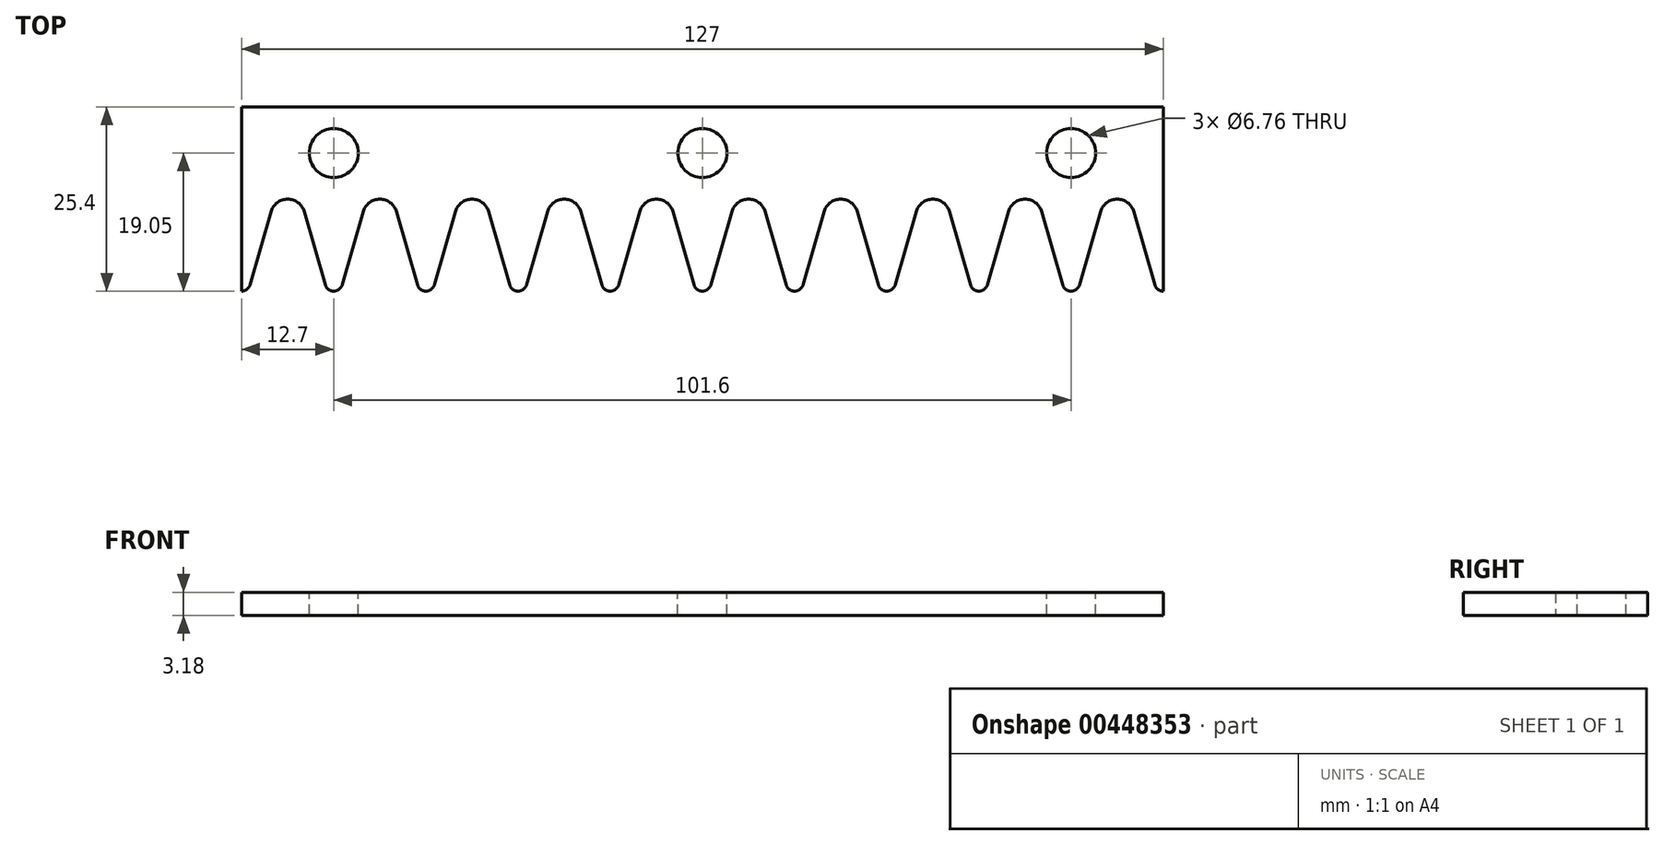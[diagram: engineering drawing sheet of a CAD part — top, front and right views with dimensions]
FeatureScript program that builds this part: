
annotation { "Feature Type Name" : "Feature", "Feature Type Description" : "" }
export const myFeature = defineFeature(function(context is Context, id is Id, definition is map)
    precondition{}
    {
        {
            var Q0;
            Q0=qCreatedBy(makeId("Top.planeOp"),FACE);
            var sketch = newSketch(context, id + "F0", { "sketchPlane" : qUnion([Q0])});
            skLineSegment(sketch, "E0.bottom", {"start": v(0, 0) * mm, "end": v(-127, 0) * mm, "construction": true});
            skLineSegment(sketch, "E0.top", {"start": v(0, 12.7) * mm, "end": v(-127, 12.7) * mm});
            skLineSegment(sketch, "E0.left", {"start": v(0, 0) * mm, "end": v(0, 12.7) * mm});
            skLineSegment(sketch, "E0.right", {"start": v(-127, 0) * mm, "end": v(-127, 12.7) * mm});
            skLineSegment(sketch, "E1", {"start": v(-127, 0) * mm, "end": v(-127, -12.7) * mm});
            skArc(sketch, "E2", {"start": v(-122.94, -1.72) * mm, "mid": v(-120.65, 0) * mm, "end": v(-118.36, -1.72) * mm});
            skLineSegment(sketch, "E3", {"start": v(-114.3, -12.7) * mm, "end": v(-114.3, 0) * mm});
            skLineSegment(sketch, "E4.1.0.0", {"start": v(-114.3, 0) * mm, "end": v(-114.3, -12.7) * mm});
            skLineSegment(sketch, "E4.direction1", {"start": v(-127, -12.7) * mm, "end": v(-114.3, -12.7) * mm, "construction": true});
            skLineSegment(sketch, "E5", {"start": v(-118.36, -1.72) * mm, "end": v(-115.44, -11.84) * mm});
            skArc(sketch, "E6", {"start": v(-125.86, -11.84) * mm, "mid": v(-126.28, -12.46) * mm, "end": v(-127, -12.7) * mm});
            skArc(sketch, "E7", {"start": v(-115.44, -11.84) * mm, "mid": v(-115.02, -12.46) * mm, "end": v(-114.3, -12.7) * mm});
            skLineSegment(sketch, "E8", {"start": v(-125.86, -11.84) * mm, "end": v(-122.94, -1.72) * mm});
            skLineSegment(sketch, "E9.1.0.1", {"start": v(-113.16, -11.84) * mm, "end": v(-110.24, -1.72) * mm});
            skArc(sketch, "E9.1.0.2", {"start": v(-110.24, -1.72) * mm, "mid": v(-107.95, 0) * mm, "end": v(-105.66, -1.72) * mm});
            skLineSegment(sketch, "E9.1.0.3", {"start": v(-105.66, -1.72) * mm, "end": v(-102.74, -11.84) * mm});
            skLineSegment(sketch, "E9.1.0.4", {"start": v(-101.6, 0) * mm, "end": v(-101.6, -12.7) * mm});
            skArc(sketch, "E9.1.0.5", {"start": v(-113.16, -11.84) * mm, "mid": v(-113.58, -12.46) * mm, "end": v(-114.3, -12.7) * mm});
            skArc(sketch, "E9.1.0.6", {"start": v(-102.74, -11.84) * mm, "mid": v(-102.32, -12.46) * mm, "end": v(-101.6, -12.7) * mm});
            skLineSegment(sketch, "E9.2.0.0", {"start": v(-101.6, 0) * mm, "end": v(-101.6, -12.7) * mm});
            skLineSegment(sketch, "E9.2.0.1", {"start": v(-100.46, -11.84) * mm, "end": v(-97.54, -1.72) * mm});
            skArc(sketch, "E9.2.0.2", {"start": v(-97.54, -1.72) * mm, "mid": v(-95.25, 0) * mm, "end": v(-92.96, -1.72) * mm});
            skLineSegment(sketch, "E9.2.0.3", {"start": v(-92.96, -1.72) * mm, "end": v(-90.04, -11.84) * mm});
            skLineSegment(sketch, "E9.2.0.4", {"start": v(-88.9, 0) * mm, "end": v(-88.9, -12.7) * mm});
            skArc(sketch, "E9.2.0.5", {"start": v(-100.46, -11.84) * mm, "mid": v(-100.88, -12.46) * mm, "end": v(-101.6, -12.7) * mm});
            skArc(sketch, "E9.2.0.6", {"start": v(-90.04, -11.84) * mm, "mid": v(-89.62, -12.46) * mm, "end": v(-88.9, -12.7) * mm});
            skLineSegment(sketch, "E9.3.0.0", {"start": v(-88.9, 0) * mm, "end": v(-88.9, -12.7) * mm});
            skLineSegment(sketch, "E9.3.0.1", {"start": v(-87.76, -11.84) * mm, "end": v(-84.84, -1.72) * mm});
            skArc(sketch, "E9.3.0.2", {"start": v(-84.84, -1.72) * mm, "mid": v(-82.55, 0) * mm, "end": v(-80.26, -1.72) * mm});
            skLineSegment(sketch, "E9.3.0.3", {"start": v(-80.26, -1.72) * mm, "end": v(-77.34, -11.84) * mm});
            skLineSegment(sketch, "E9.3.0.4", {"start": v(-76.2, 0) * mm, "end": v(-76.2, -12.7) * mm});
            skArc(sketch, "E9.3.0.5", {"start": v(-87.76, -11.84) * mm, "mid": v(-88.18, -12.46) * mm, "end": v(-88.9, -12.7) * mm});
            skArc(sketch, "E9.3.0.6", {"start": v(-77.34, -11.84) * mm, "mid": v(-76.92, -12.46) * mm, "end": v(-76.2, -12.7) * mm});
            skLineSegment(sketch, "E9.4.0.0", {"start": v(-76.2, 0) * mm, "end": v(-76.2, -12.7) * mm});
            skLineSegment(sketch, "E9.4.0.1", {"start": v(-75.06, -11.84) * mm, "end": v(-72.14, -1.72) * mm});
            skArc(sketch, "E9.4.0.2", {"start": v(-72.14, -1.72) * mm, "mid": v(-69.85, 0) * mm, "end": v(-67.56, -1.72) * mm});
            skLineSegment(sketch, "E9.4.0.3", {"start": v(-67.56, -1.72) * mm, "end": v(-64.64, -11.84) * mm});
            skLineSegment(sketch, "E9.4.0.4", {"start": v(-63.5, 0) * mm, "end": v(-63.5, -12.7) * mm});
            skArc(sketch, "E9.4.0.5", {"start": v(-75.06, -11.84) * mm, "mid": v(-75.48, -12.46) * mm, "end": v(-76.2, -12.7) * mm});
            skArc(sketch, "E9.4.0.6", {"start": v(-64.64, -11.84) * mm, "mid": v(-64.22, -12.46) * mm, "end": v(-63.5, -12.7) * mm});
            skLineSegment(sketch, "E9.5.0.0", {"start": v(-63.5, 0) * mm, "end": v(-63.5, -12.7) * mm});
            skLineSegment(sketch, "E9.5.0.1", {"start": v(-62.36, -11.84) * mm, "end": v(-59.44, -1.72) * mm});
            skArc(sketch, "E9.5.0.2", {"start": v(-59.44, -1.72) * mm, "mid": v(-57.15, 0) * mm, "end": v(-54.86, -1.72) * mm});
            skLineSegment(sketch, "E9.5.0.3", {"start": v(-54.86, -1.72) * mm, "end": v(-51.94, -11.84) * mm});
            skLineSegment(sketch, "E9.5.0.4", {"start": v(-50.8, 0) * mm, "end": v(-50.8, -12.7) * mm});
            skArc(sketch, "E9.5.0.5", {"start": v(-62.36, -11.84) * mm, "mid": v(-62.78, -12.46) * mm, "end": v(-63.5, -12.7) * mm});
            skArc(sketch, "E9.5.0.6", {"start": v(-51.94, -11.84) * mm, "mid": v(-51.52, -12.46) * mm, "end": v(-50.8, -12.7) * mm});
            skLineSegment(sketch, "E9.6.0.0", {"start": v(-50.8, 0) * mm, "end": v(-50.8, -12.7) * mm});
            skLineSegment(sketch, "E9.6.0.1", {"start": v(-49.66, -11.84) * mm, "end": v(-46.74, -1.72) * mm});
            skArc(sketch, "E9.6.0.2", {"start": v(-46.74, -1.72) * mm, "mid": v(-44.45, 0) * mm, "end": v(-42.16, -1.72) * mm});
            skLineSegment(sketch, "E9.6.0.3", {"start": v(-42.16, -1.72) * mm, "end": v(-39.24, -11.84) * mm});
            skLineSegment(sketch, "E9.6.0.4", {"start": v(-38.1, 0) * mm, "end": v(-38.1, -12.7) * mm});
            skArc(sketch, "E9.6.0.5", {"start": v(-49.66, -11.84) * mm, "mid": v(-50.08, -12.46) * mm, "end": v(-50.8, -12.7) * mm});
            skArc(sketch, "E9.6.0.6", {"start": v(-39.24, -11.84) * mm, "mid": v(-38.82, -12.46) * mm, "end": v(-38.1, -12.7) * mm});
            skLineSegment(sketch, "E9.7.0.0", {"start": v(-38.1, 0) * mm, "end": v(-38.1, -12.7) * mm});
            skLineSegment(sketch, "E9.7.0.1", {"start": v(-36.96, -11.84) * mm, "end": v(-34.04, -1.72) * mm});
            skArc(sketch, "E9.7.0.2", {"start": v(-34.04, -1.72) * mm, "mid": v(-31.75, 0) * mm, "end": v(-29.46, -1.72) * mm});
            skLineSegment(sketch, "E9.7.0.3", {"start": v(-29.46, -1.72) * mm, "end": v(-26.54, -11.84) * mm});
            skLineSegment(sketch, "E9.7.0.4", {"start": v(-25.4, 0) * mm, "end": v(-25.4, -12.7) * mm});
            skArc(sketch, "E9.7.0.5", {"start": v(-36.96, -11.84) * mm, "mid": v(-37.38, -12.46) * mm, "end": v(-38.1, -12.7) * mm});
            skArc(sketch, "E9.7.0.6", {"start": v(-26.54, -11.84) * mm, "mid": v(-26.12, -12.46) * mm, "end": v(-25.4, -12.7) * mm});
            skLineSegment(sketch, "E9.8.0.0", {"start": v(-25.4, 0) * mm, "end": v(-25.4, -12.7) * mm});
            skLineSegment(sketch, "E9.8.0.1", {"start": v(-24.26, -11.84) * mm, "end": v(-21.34, -1.72) * mm});
            skArc(sketch, "E9.8.0.2", {"start": v(-21.34, -1.72) * mm, "mid": v(-19.05, 0) * mm, "end": v(-16.76, -1.72) * mm});
            skLineSegment(sketch, "E9.8.0.3", {"start": v(-16.76, -1.72) * mm, "end": v(-13.84, -11.84) * mm});
            skLineSegment(sketch, "E9.8.0.4", {"start": v(-12.7, 0) * mm, "end": v(-12.7, -12.7) * mm});
            skArc(sketch, "E9.8.0.5", {"start": v(-24.26, -11.84) * mm, "mid": v(-24.68, -12.46) * mm, "end": v(-25.4, -12.7) * mm});
            skArc(sketch, "E9.8.0.6", {"start": v(-13.84, -11.84) * mm, "mid": v(-13.42, -12.46) * mm, "end": v(-12.7, -12.7) * mm});
            skLineSegment(sketch, "E9.9.0.0", {"start": v(-12.7, 0) * mm, "end": v(-12.7, -12.7) * mm});
            skLineSegment(sketch, "E9.9.0.1", {"start": v(-11.56, -11.84) * mm, "end": v(-8.64, -1.72) * mm});
            skArc(sketch, "E9.9.0.2", {"start": v(-8.64, -1.72) * mm, "mid": v(-6.35, 0) * mm, "end": v(-4.06, -1.72) * mm});
            skLineSegment(sketch, "E9.9.0.3", {"start": v(-4.06, -1.72) * mm, "end": v(-1.14, -11.84) * mm});
            skLineSegment(sketch, "E9.9.0.4", {"start": v(0, 0) * mm, "end": v(0, -12.7) * mm});
            skArc(sketch, "E9.9.0.5", {"start": v(-11.56, -11.84) * mm, "mid": v(-11.98, -12.46) * mm, "end": v(-12.7, -12.7) * mm});
            skArc(sketch, "E9.9.0.6", {"start": v(-1.14, -11.84) * mm, "mid": v(-0.72, -12.46) * mm, "end": v(0, -12.7) * mm});
            skSolve(sketch);
        }
        {
            var Q0;
            Q0=makeQuery(id+"F0.imprint","IMPRINT",FACE,{"disambiguationData":[TD([[makeQuery(id+"F0.imprint","IMPRINT",EDGE,{"derivedFrom":sQuery(id+"F0.wireOp",EDGE,"E0.top")}),1.0]])]});
            extrude(context, id + "F1", {"entities" : qUnion([Q0]), "depth" : 3.17 * mm});
        }
        {
            var Q0;
            Q0=makeQuery(id+"F1.opExtrude","CAP_FACE",FACE,{"disambiguationData":[OSD([sQuery(id+"F0.wireOp",EDGE,"E0.top"),sQuery(id+"F0.wireOp",EDGE,"E0.left"),sQuery(id+"F0.wireOp",EDGE,"E0.right"),sQuery(id+"F0.wireOp",EDGE,"E1"),sQuery(id+"F0.wireOp",EDGE,"PW4FySWp-zVU2-GpDa-Lfng-2MmFDWqlCH1t"),sQuery(id+"F0.wireOp",EDGE,"CtuzIzuM-RDB8-6xeh-k4E4-42BdhT9GvzJf"),sQuery(id+"F0.wireOp",EDGE,"E2"),sQuery(id+"F0.wireOp",EDGE,"apolegve-J87E-izKM-QJrC-zitneBt8YgNK"),sQuery(id+"F0.wireOp",EDGE,"PiZquHoN-DRwv-tvar-NRW5-UBCCp7MdhKiI"),sQuery(id+"F0.wireOp",EDGE,"E4.1.0.1"),sQuery(id+"F0.wireOp",EDGE,"E4.1.0.2"),sQuery(id+"F0.wireOp",EDGE,"E4.1.0.3"),sQuery(id+"F0.wireOp",EDGE,"E4.1.0.4"),sQuery(id+"F0.wireOp",EDGE,"E4.1.0.5"),sQuery(id+"F0.wireOp",EDGE,"E4.2.0.1"),sQuery(id+"F0.wireOp",EDGE,"E4.2.0.2"),sQuery(id+"F0.wireOp",EDGE,"E4.2.0.3"),sQuery(id+"F0.wireOp",EDGE,"E4.2.0.4"),sQuery(id+"F0.wireOp",EDGE,"E4.2.0.5"),sQuery(id+"F0.wireOp",EDGE,"E4.3.0.1"),sQuery(id+"F0.wireOp",EDGE,"E4.3.0.2"),sQuery(id+"F0.wireOp",EDGE,"E4.3.0.3"),sQuery(id+"F0.wireOp",EDGE,"E4.3.0.4"),sQuery(id+"F0.wireOp",EDGE,"E4.3.0.5"),sQuery(id+"F0.wireOp",EDGE,"E4.4.0.1"),sQuery(id+"F0.wireOp",EDGE,"E4.4.0.2"),sQuery(id+"F0.wireOp",EDGE,"E4.4.0.3"),sQuery(id+"F0.wireOp",EDGE,"E4.4.0.4"),sQuery(id+"F0.wireOp",EDGE,"E4.4.0.5"),sQuery(id+"F0.wireOp",EDGE,"E4.5.0.1"),sQuery(id+"F0.wireOp",EDGE,"E4.5.0.2"),sQuery(id+"F0.wireOp",EDGE,"E4.5.0.3"),sQuery(id+"F0.wireOp",EDGE,"E4.5.0.4"),sQuery(id+"F0.wireOp",EDGE,"E4.5.0.5"),sQuery(id+"F0.wireOp",EDGE,"E4.6.0.1"),sQuery(id+"F0.wireOp",EDGE,"E4.6.0.2"),sQuery(id+"F0.wireOp",EDGE,"E4.6.0.3"),sQuery(id+"F0.wireOp",EDGE,"E4.6.0.4"),sQuery(id+"F0.wireOp",EDGE,"E4.6.0.5"),sQuery(id+"F0.wireOp",EDGE,"E4.7.0.1"),sQuery(id+"F0.wireOp",EDGE,"E4.7.0.2"),sQuery(id+"F0.wireOp",EDGE,"E4.7.0.3"),sQuery(id+"F0.wireOp",EDGE,"E4.7.0.4"),sQuery(id+"F0.wireOp",EDGE,"E4.7.0.5"),sQuery(id+"F0.wireOp",EDGE,"E4.8.0.1"),sQuery(id+"F0.wireOp",EDGE,"E4.8.0.2"),sQuery(id+"F0.wireOp",EDGE,"E4.8.0.3"),sQuery(id+"F0.wireOp",EDGE,"E4.8.0.4"),sQuery(id+"F0.wireOp",EDGE,"E4.8.0.5"),sQuery(id+"F0.wireOp",EDGE,"E4.9.0.1"),sQuery(id+"F0.wireOp",EDGE,"E4.9.0.2"),sQuery(id+"F0.wireOp",EDGE,"E4.9.0.3"),sQuery(id+"F0.wireOp",EDGE,"E4.9.0.4"),sQuery(id+"F0.wireOp",EDGE,"E4.9.0.5"),sQuery(id+"F0.wireOp",EDGE,"Xy6wUBCt-IeAr-GLyQ-Hadt-AkeyYF98njrb")])],"isStart":false});
            var sketch = newSketch(context, id + "F2", { "sketchPlane" : qUnion([Q0])});
            skPoint(sketch, "E10", {"position": v(-114.3, 6.35) * mm});
            skPoint(sketch, "E11.1.0.0", {"position": v(-63.5, 6.35) * mm});
            skPoint(sketch, "E11.2.0.0", {"position": v(-12.7, 6.35) * mm});
            skLineSegment(sketch, "E11.direction1", {"start": v(-114.3, 6.35) * mm, "end": v(-63.5, 6.35) * mm, "construction": true});
            skSolve(sketch);
        }
        {
            var Q0;
            Q0=sQuery(id+"F2.wireOp",VERTEX,"E10");
            var Q1;
            Q1=sQuery(id+"F2.wireOp",VERTEX,"E11.1.0.0");
            var Q2;
            Q2=sQuery(id+"F2.wireOp",VERTEX,"E11.2.0.0");
            var Q3;
            Q3=sQuery(id+"F2.wireOp",VERTEX,"E11.3.0.0");
            var Q4;
            Q4=sQuery(id+"F2.wireOp",VERTEX,"E11.4.0.0");
            var Q5;
            Q5=makeQuery(id+"F1.opExtrude","SWEPT_BODY",BODY,{"disambiguationData":[OSD([sQuery(id+"F0.wireOp",EDGE,"E0.top"),sQuery(id+"F0.wireOp",EDGE,"E0.left"),sQuery(id+"F0.wireOp",EDGE,"E0.right"),sQuery(id+"F0.wireOp",EDGE,"E1"),sQuery(id+"F0.wireOp",EDGE,"PW4FySWp-zVU2-GpDa-Lfng-2MmFDWqlCH1t"),sQuery(id+"F0.wireOp",EDGE,"CtuzIzuM-RDB8-6xeh-k4E4-42BdhT9GvzJf"),sQuery(id+"F0.wireOp",EDGE,"E2"),sQuery(id+"F0.wireOp",EDGE,"apolegve-J87E-izKM-QJrC-zitneBt8YgNK"),sQuery(id+"F0.wireOp",EDGE,"PiZquHoN-DRwv-tvar-NRW5-UBCCp7MdhKiI"),sQuery(id+"F0.wireOp",EDGE,"E4.1.0.1"),sQuery(id+"F0.wireOp",EDGE,"E4.1.0.2"),sQuery(id+"F0.wireOp",EDGE,"E4.1.0.3"),sQuery(id+"F0.wireOp",EDGE,"E4.1.0.4"),sQuery(id+"F0.wireOp",EDGE,"E4.1.0.5"),sQuery(id+"F0.wireOp",EDGE,"E4.2.0.1"),sQuery(id+"F0.wireOp",EDGE,"E4.2.0.2"),sQuery(id+"F0.wireOp",EDGE,"E4.2.0.3"),sQuery(id+"F0.wireOp",EDGE,"E4.2.0.4"),sQuery(id+"F0.wireOp",EDGE,"E4.2.0.5"),sQuery(id+"F0.wireOp",EDGE,"E4.3.0.1"),sQuery(id+"F0.wireOp",EDGE,"E4.3.0.2"),sQuery(id+"F0.wireOp",EDGE,"E4.3.0.3"),sQuery(id+"F0.wireOp",EDGE,"E4.3.0.4"),sQuery(id+"F0.wireOp",EDGE,"E4.3.0.5"),sQuery(id+"F0.wireOp",EDGE,"E4.4.0.1"),sQuery(id+"F0.wireOp",EDGE,"E4.4.0.2"),sQuery(id+"F0.wireOp",EDGE,"E4.4.0.3"),sQuery(id+"F0.wireOp",EDGE,"E4.4.0.4"),sQuery(id+"F0.wireOp",EDGE,"E4.4.0.5"),sQuery(id+"F0.wireOp",EDGE,"E4.5.0.1"),sQuery(id+"F0.wireOp",EDGE,"E4.5.0.2"),sQuery(id+"F0.wireOp",EDGE,"E4.5.0.3"),sQuery(id+"F0.wireOp",EDGE,"E4.5.0.4"),sQuery(id+"F0.wireOp",EDGE,"E4.5.0.5"),sQuery(id+"F0.wireOp",EDGE,"E4.6.0.1"),sQuery(id+"F0.wireOp",EDGE,"E4.6.0.2"),sQuery(id+"F0.wireOp",EDGE,"E4.6.0.3"),sQuery(id+"F0.wireOp",EDGE,"E4.6.0.4"),sQuery(id+"F0.wireOp",EDGE,"E4.6.0.5"),sQuery(id+"F0.wireOp",EDGE,"E4.7.0.1"),sQuery(id+"F0.wireOp",EDGE,"E4.7.0.2"),sQuery(id+"F0.wireOp",EDGE,"E4.7.0.3"),sQuery(id+"F0.wireOp",EDGE,"E4.7.0.4"),sQuery(id+"F0.wireOp",EDGE,"E4.7.0.5"),sQuery(id+"F0.wireOp",EDGE,"E4.8.0.1"),sQuery(id+"F0.wireOp",EDGE,"E4.8.0.2"),sQuery(id+"F0.wireOp",EDGE,"E4.8.0.3"),sQuery(id+"F0.wireOp",EDGE,"E4.8.0.4"),sQuery(id+"F0.wireOp",EDGE,"E4.8.0.5"),sQuery(id+"F0.wireOp",EDGE,"E4.9.0.1"),sQuery(id+"F0.wireOp",EDGE,"E4.9.0.2"),sQuery(id+"F0.wireOp",EDGE,"E4.9.0.3"),sQuery(id+"F0.wireOp",EDGE,"E4.9.0.4"),sQuery(id+"F0.wireOp",EDGE,"E4.9.0.5"),sQuery(id+"F0.wireOp",EDGE,"Xy6wUBCt-IeAr-GLyQ-Hadt-AkeyYF98njrb")])]});
            hole(context, id + "F3", {"style" : HoleStyle.SIMPLE, "endStyle" : HoleEndStyle.THROUGH, "standardTappedOrClearance" : lookupTablePath({ "standard" : "ANSI", "fit" : "Normal (ASME)", "size" : "1/4", "type" : "Clearance" }), "standardBlindInLast" : lookupTablePath({ "fit" : "Free", "standard" : "ANSI", "size" : "1/4", "type" : "Clearance" }), "holeDiameter" : 6.76 * mm, "isTappedThrough" : true, "tappedDepth" : 12.7 * mm, "tapClearance" : 3, "locations" : qUnion([Q0, Q1, Q2, Q3, Q4]), "scope" : qUnion([Q5])});
        }
    });
